# Revit family: Sink-Pedestal-KOHLER-Memoirs-K-2267T_1
name_source: partatom
category: Specialty Equipment
units: mm (PartAtom-declared; Revit-internal decimal feet)

## family parameters
Cut with Voids When Loaded = No
Host = Face
OmniClass Number = 23.31.25.00
OmniClass Title = Toilet and Bath Specialties
Part Type = Normal
Room Calculation Point = No
Round Connector Dimension = Use Diameter
Shared = No

## types (4) — shared parameters
ADA Compliant = No
Assembly Code = C1030200
Date Modified = 05/26/2023
Default Elevation = 0"
Description = Pedestal
Height = 27 1/2"
Length = 11 1/16"
Manufacturer = Kohler Co.
Master Format 2014 = 10 28 00
Master Format 2014 Name = Toilet, Bath, and Laundry Accessories
Material = Fireclay
Product Name = Memoirs
URL = http://www.kohler.com.cn
WaterSense Certified = No
Width = 10 1/8"

## per-type parameters (varying)
| type | Finish | Model | Type |
| 0-White | KOHLER-Fireclay-0-White | K-2267T-0 | 1 |
| 96-Biscuit | KOHLER-Fireclay-96-Biscuit | K-2267T-96 | 2 |
| H15-Spring Green | KOHLER-Fireclay-H15-Spring_Green | K-2267T-H15 | 3 |
| V10-Peachblow | KOHLER-Fireclay-V10-Peachblow | K-2267T-V10 | 4 |

## geometry (parser evidence)
native form markers: Sweep x5
no freeform markers — native parametric forms only
